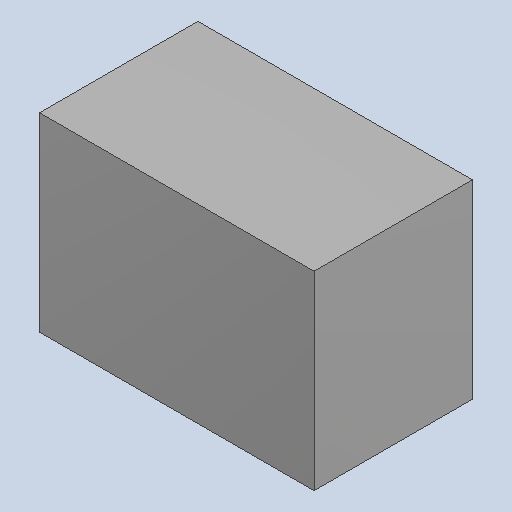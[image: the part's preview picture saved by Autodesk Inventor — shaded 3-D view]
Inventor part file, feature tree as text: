
AUTODESK INVENTOR PART (.ipt)
format: ipt  version: 2023.4 (Build 274418000, 418)  size: 82,432 bytes
history: native  units: mm
features: extrude x1
ambient origin geometry x8: Origin, YZ Plane, XZ Plane, XY Plane, X Axis, Y Axis, Z Axis, Center Point
bodies: Solid1 (feature_tree)
feature tree (1):
  extrude  "Extruded_3"  [1 undecoded]
note: 1 required parameter value undecoded (feature->parameter linkage not recoverable at this tier; creation-order binding heuristic only, values carry confidence <= 0.55)
